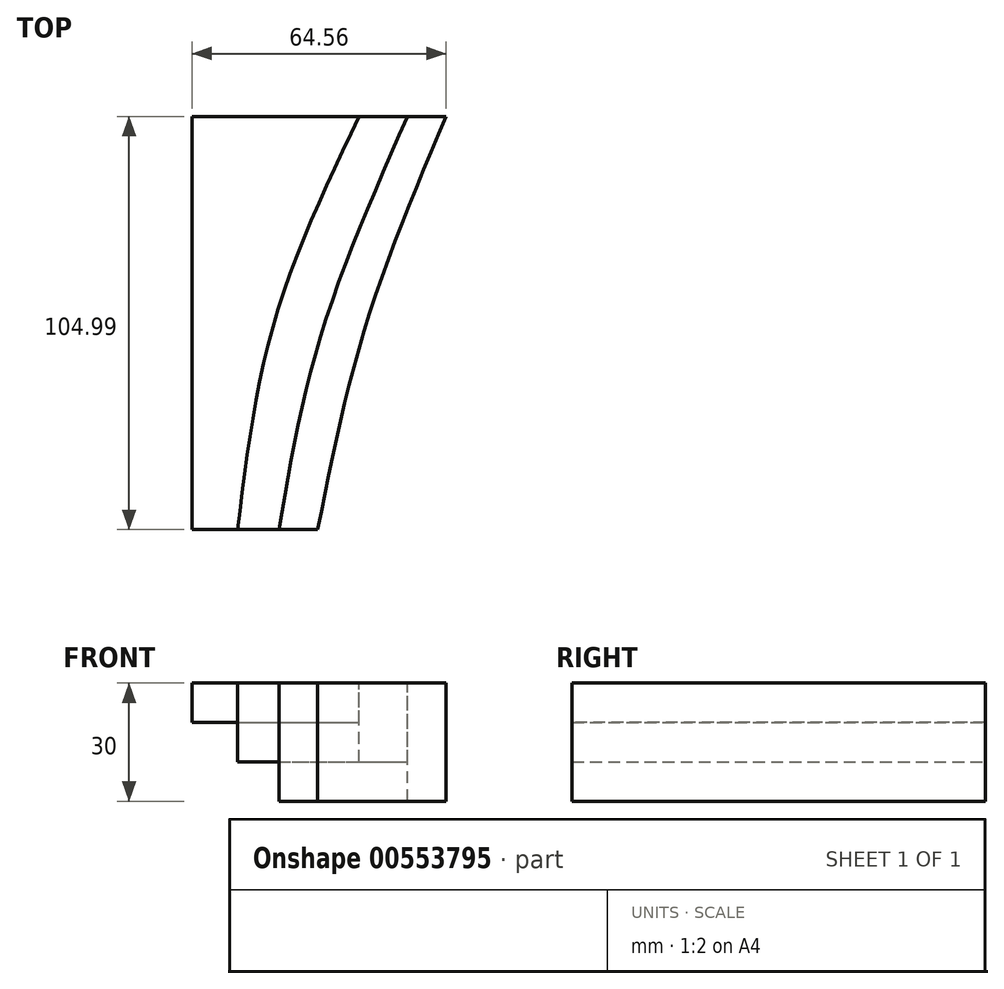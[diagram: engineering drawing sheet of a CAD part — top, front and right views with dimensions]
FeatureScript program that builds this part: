
annotation { "Feature Type Name" : "Feature", "Feature Type Description" : "" }
export const myFeature = defineFeature(function(context is Context, id is Id, definition is map)
    precondition{}
    {
        {
            var Q0;
            Q0=qCreatedBy(makeId("Top.planeOp"),FACE);
            var sketch = newSketch(context, id + "F0", { "sketchPlane" : qUnion([Q0])});
            skLineSegment(sketch, "E0.bottom", {"start": v(-30, 24.03) * mm, "end": v(-20, 24.03) * mm});
            skLineSegment(sketch, "E0.top", {"start": v(-30, 14.03) * mm, "end": v(-20, 14.03) * mm});
            skLineSegment(sketch, "E0.left", {"start": v(-30, 24.03) * mm, "end": v(-30, 14.03) * mm});
            skLineSegment(sketch, "E0.right", {"start": v(-20, 24.03) * mm, "end": v(-20, 14.03) * mm});
            skLineSegment(sketch, "E1.bottom", {"start": v(-30, 14.03) * mm, "end": v(-10, 14.03) * mm});
            skLineSegment(sketch, "E1.top", {"start": v(-30, 35.34) * mm, "end": v(-10, 35.34) * mm});
            skLineSegment(sketch, "E1.left", {"start": v(-30, 14.03) * mm, "end": v(-30, 35.34) * mm});
            skLineSegment(sketch, "E1.right", {"start": v(-10, 14.03) * mm, "end": v(-10, 35.34) * mm});
            skLineSegment(sketch, "E2.bottom", {"start": v(-30, 14.03) * mm, "end": v(0, 14.03) * mm});
            skLineSegment(sketch, "E2.top", {"start": v(-30, 48.25) * mm, "end": v(0, 48.25) * mm});
            skLineSegment(sketch, "E2.left", {"start": v(-30, 14.03) * mm, "end": v(-30, 48.25) * mm});
            skLineSegment(sketch, "E2.right", {"start": v(0, 14.03) * mm, "end": v(0, 48.25) * mm});
            skLineSegment(sketch, "E3.bottom", {"start": v(-30, 14.03) * mm, "end": v(10, 14.03) * mm});
            skLineSegment(sketch, "E3.top", {"start": v(-30, 60.82) * mm, "end": v(10, 60.82) * mm});
            skLineSegment(sketch, "E3.left", {"start": v(-30, 14.03) * mm, "end": v(-30, 60.82) * mm});
            skLineSegment(sketch, "E3.right", {"start": v(10, 14.03) * mm, "end": v(10, 60.82) * mm});
            skLineSegment(sketch, "E4.bottom", {"start": v(-30, 14.03) * mm, "end": v(20, 14.03) * mm});
            skLineSegment(sketch, "E4.top", {"start": v(-30, 71.7) * mm, "end": v(20, 71.7) * mm});
            skLineSegment(sketch, "E4.left", {"start": v(-30, 14.03) * mm, "end": v(-30, 71.7) * mm});
            skLineSegment(sketch, "E4.right", {"start": v(20, 14.03) * mm, "end": v(20, 71.7) * mm});
            skLineSegment(sketch, "E5.bottom", {"start": v(-30, 14.03) * mm, "end": v(30, 14.03) * mm});
            skLineSegment(sketch, "E5.top", {"start": v(-30, 81.55) * mm, "end": v(30, 81.55) * mm});
            skLineSegment(sketch, "E5.left", {"start": v(-30, 14.03) * mm, "end": v(-30, 81.55) * mm});
            skLineSegment(sketch, "E5.right", {"start": v(30, 14.03) * mm, "end": v(30, 81.55) * mm});
            skLineSegment(sketch, "E6.bottom", {"start": v(-30, 14.03) * mm, "end": v(40, 14.03) * mm});
            skLineSegment(sketch, "E6.top", {"start": v(-30, 91.07) * mm, "end": v(40, 91.07) * mm});
            skLineSegment(sketch, "E6.left", {"start": v(-30, 14.03) * mm, "end": v(-30, 91.07) * mm});
            skLineSegment(sketch, "E6.right", {"start": v(40, 14.03) * mm, "end": v(40, 91.07) * mm});
            skLineSegment(sketch, "E7.bottom", {"start": v(-198.27, 28.2) * mm, "end": v(-75.26, 28.2) * mm});
            skLineSegment(sketch, "E7.top", {"start": v(-198.27, -76.8) * mm, "end": v(-75.26, -76.8) * mm});
            skLineSegment(sketch, "E7.left", {"start": v(-198.27, 28.2) * mm, "end": v(-198.27, -76.8) * mm});
            skLineSegment(sketch, "E7.right", {"start": v(-75.26, 28.2) * mm, "end": v(-75.26, -76.8) * mm});
            skFitSpline(sketch, "E8", {"points": [v(-186.72, -76.8) * mm, v(-177.2, -23.45) * mm, v(-155.8, 28.2) * mm], "startDerivative": vector(13.4, 108.79) * mm, "endDerivative": vector(48.35, 101.23) * mm});
            skFitSpline(sketch, "E9", {"points": [v(-176.18, -76.8) * mm, v(-165.65, -27.86) * mm, v(-143.56, 28.2) * mm], "startDerivative": vector(17.3, 101.54) * mm, "endDerivative": vector(47.48, 108.35) * mm});
            skFitSpline(sketch, "E10", {"points": [v(-166.33, -76.8) * mm, v(-154.1, -24.8) * mm, v(-133.7, 28.2) * mm], "startDerivative": vector(21.08, 105.9) * mm, "endDerivative": vector(44.05, 104.11) * mm});
            skFitSpline(sketch, "E11", {"points": [v(-157.5, -76.8) * mm, v(-143.22, -22.43) * mm, v(-122.16, 28.2) * mm], "startDerivative": vector(24.84, 109.62) * mm, "endDerivative": vector(45.88, 100.35) * mm});
            skFitSpline(sketch, "E12", {"points": [v(-147.3, -76.8) * mm, v(-133.7, -29.22) * mm, v(-110.6, 28.2) * mm], "startDerivative": vector(25.26, 98.9) * mm, "endDerivative": vector(47.72, 110.87) * mm});
            skFitSpline(sketch, "E13", {"points": [v(-139.83, -76.8) * mm, v(-123.52, -26.16) * mm, v(-99.73, 28.2) * mm], "startDerivative": vector(33.07, 94.26) * mm, "endDerivative": vector(46.8, 115.22) * mm});
            skFitSpline(sketch, "E14", {"points": [v(-133.7, -76.8) * mm, v(-122.16, -53.69) * mm, v(-110.6, -76.8) * mm], "startDerivative": vector(17.51, 73.8) * mm, "endDerivative": vector(28.64, -73.02) * mm});
            skSolve(sketch);
        }
        {
            var Q0;
            {var subQ0=sQuery(id+"F0.wireOp",EDGE,"E7.left");Q0=makeQuery(id+"F0.imprint","IMPRINT",FACE,{"disambiguationData":[TD([[makeQuery(id+"F0.imprint","IMPRINT",EDGE,{"derivedFrom":subQ0}),1.0]])]});}
            extrude(context, id + "F1", {"entities" : qUnion([Q0]), "oppositeDirection" : true, "depth" : 10 * mm, "offsetDistance" : 25 * mm});
        }
        {
            var Q0;
            {var subQ0=sQuery(id+"F0.wireOp",EDGE,"E8");Q0=makeQuery(id+"F0.imprint","IMPRINT",FACE,{"disambiguationData":[TD([[makeQuery(id+"F0.imprint","IMPRINT",EDGE,{"derivedFrom":subQ0}),-1.0]])]});}
            extrude(context, id + "F2", {"entities" : qUnion([Q0]), "oppositeDirection" : true, "depth" : 20 * mm, "offsetDistance" : 25 * mm});
        }
        {
            var Q0;
            {var subQ0=sQuery(id+"F0.wireOp",EDGE,"E9");Q0=makeQuery(id+"F0.imprint","IMPRINT",FACE,{"disambiguationData":[TD([[makeQuery(id+"F0.imprint","IMPRINT",EDGE,{"derivedFrom":subQ0}),-1.0]])]});}
            extrude(context, id + "F3", {"entities" : qUnion([Q0]), "oppositeDirection" : true, "depth" : 30 * mm, "offsetDistance" : 25 * mm});
        }
    });
